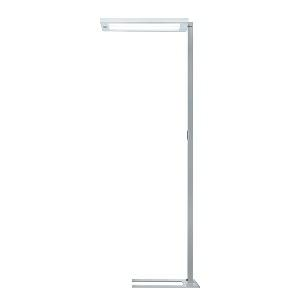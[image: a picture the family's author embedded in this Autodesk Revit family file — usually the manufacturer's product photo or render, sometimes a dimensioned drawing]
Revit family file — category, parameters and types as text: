
# Revit family: lavigo_-_dps_9000_840_r_g2_00803364_ba93
name_source: partatom
category: Lighting Fixtures
units: mm (PartAtom-declared; Revit-internal decimal feet)

## family parameters
Cut with Voids When Loaded = No
Host = Face
Light Source = No
Part Type = Normal
Room Calculation Point = No
Round Connector Dimension = Use Diameter
Shared = No

## types (1)
- LAVIGO - DPS 9000/840/R/G2 (1 x LED, 8950 lm, 4000K)
    Apparent Load = 63 VA
    Approval mark = CE
    CIE Flux Codes = 60 87 97 20 100
    Color Rendering = 80-89
    Color Temperature = 4000K
    Control Gear = Electronic ballast
    Default Elevation = 1800 mm
    Description = DPS 9000/840/R/G2|Free-standing luminaire|light source: LED|work equipment: Electronic ballast|connected load: 220-240 V, 50/60 Hz|Power consumption: approx. 63 W|standby: approx. 0,50|power factor: approx. 0,910|luminous flux: 8950 lm|luminous efficacy: 142 lm/W|light distribution: Direct/indirect|direct ratio: approx. 20 %|colour temperature: Cold white, ca. 4000 K|color rendering index (CRI): >= 80|chromaticity tolerance:  3 SDCM|technology: Presence and daylight sensor control (PIR)|operation: Multi-function switch|luminaire body|material: Steel/plastic|surface: Painted|colour: Silver metallic|lamp cover: Acrylic (PMMA), Satine|tubular section|material: Steel tube|surface: Painted|Form: Tubular section upright|colour of tubular section: Silver metallic|luminaire base|Form: C-form flat|weight (net): approx. 19.7 kg|mains lead: 3.00 m Mains plug CEE 7/VII|Fastening: Floor standing base|decorative contrast side parts: Flint grey|glare control: Prism aperture|luminance(L65): <= 3000 cd/m|unified glare rating(4H 8H): <=  16|special features: Luminaire head detachable, Cradle to Cradle Certified TM, Direct light component with edge light and light-guide technology for homogenous light exit, Flicker-free, Integrated light and presence sensor PIR, Retrofittable with TALK module, Separated, direct and indirect light individually adjustable|
    Frequency = 50 Hz
    Height = 36 mm
    Lamp = 1 x LED
    Lamp Light Flux = 8950 lm
    Lamp count = 1
    Length = 675 mm
    Luminous efficacy = 142 lm/W
    Manufacturer = Waldmann
    ModVariant = No
    Model = 00803364
    Mounting Place = Floor
    Mounting Type = Freestanding
    Number of Poles = 1
    OnlyDefault = Yes
    Power Factor = 1
    Product Name = LAVIGO - DPS 9000/840/R/G2
    Product group = Free standing luminaire
    ProductGroupID = 13
    Protection Class = Protection class I
    Protection Degree = IP 20
    RLX_Detail_Level = 1
    RLX_Emergency_Light_Flux = 0 lm
    RLX_Emergency_Type = 0
    RLX_Emergency_Type_DB = No
    RlxData = <blob elided: 37837 chars, md5=e13e2c03>
    Socket = socket
    Standby Power = 0 W
    System Light Flux = 8950 lm
    System Power = 63 W
    Type Comments = Product without accessories
    Type Image = 121695000-00625713.jpg
    URL = http://relux.com
    VarID = ---
    Voltage = 230 V
    Voltage Range = 220-240 V
    Weight = 0.00 kg
    Width = 320 mm

## geometry (parser evidence)
native form markers: Blend x4, Sweep x13
no freeform markers — native parametric forms only
